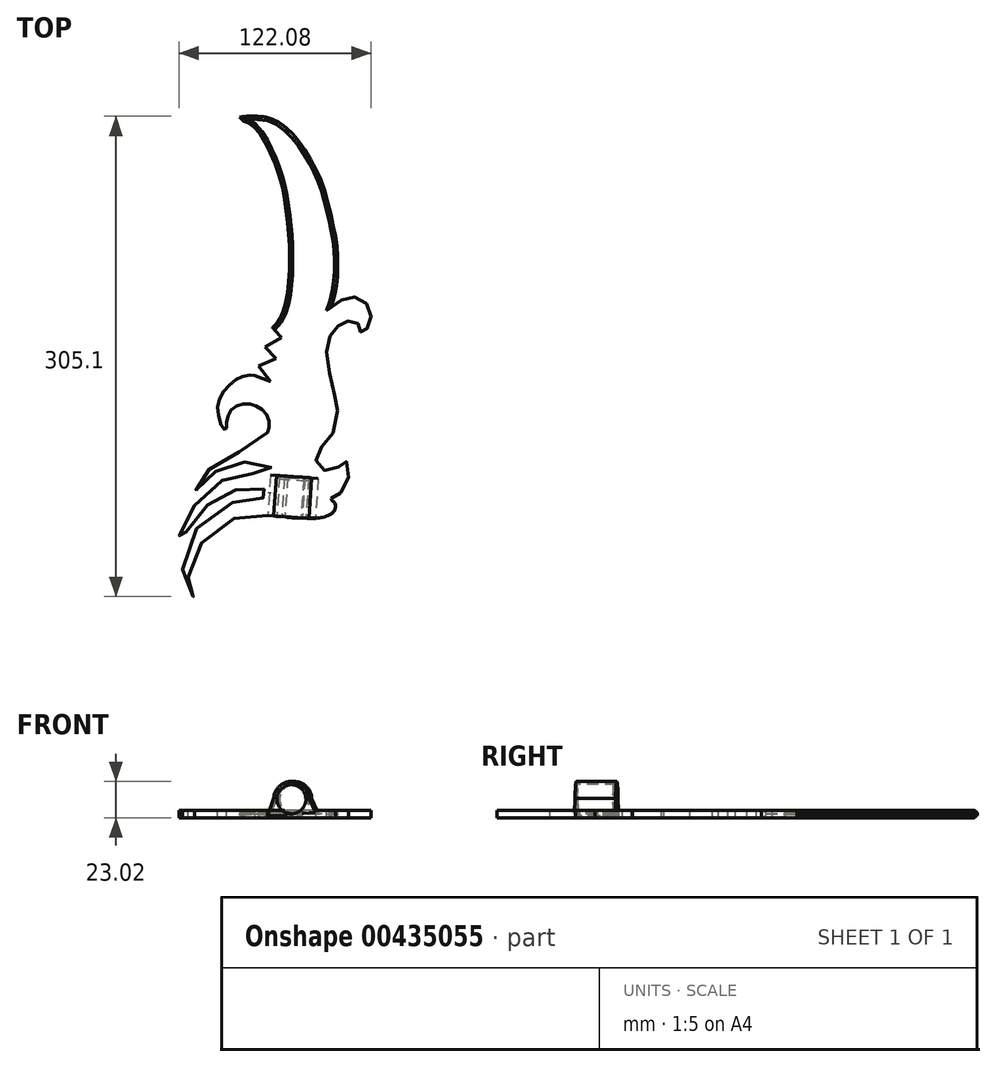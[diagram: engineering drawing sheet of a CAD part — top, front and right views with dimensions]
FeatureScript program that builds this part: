
annotation { "Feature Type Name" : "Feature", "Feature Type Description" : "" }
export const myFeature = defineFeature(function(context is Context, id is Id, definition is map)
    precondition{}
    {
        {
            var Q0;
            Q0=qCreatedBy(makeId("Top.planeOp"),FACE);
            var sketch = newSketch(context, id + "F0", { "sketchPlane" : qUnion([Q0])});
            skFitSpline(sketch, "E0", {"points": [v(-34.12, 66.89) * mm, v(-30.2, 66.33) * mm, v(-25.4, 63.2) * mm, v(-21.03, 57.83) * mm, v(-16.78, 49.66) * mm, v(-14.1, 40.04) * mm, v(-12.64, 32.43) * mm, v(-12.52, 25.04) * mm, v(-13.23, 19.62) * mm, v(-14.2, 16.34) * mm], "startDerivative": vector(44.42, -1.57) * mm, "endDerivative": vector(-12.95, -38.23) * mm});
            skPoint(sketch, "E1.1.internal.orphan", {"position": v(-37.5, 65.72) * mm});
            skFitSpline(sketch, "E2", {"points": [v(-38.79, 67.2) * mm, v(-37.5, 65.72) * mm, v(-36.06, 65.1) * mm, v(-33.67, 63.13) * mm, v(-30.7, 58) * mm, v(-27.58, 49.9) * mm, v(-26.1, 41.97) * mm, v(-25.34, 34.51) * mm, v(-25.23, 26.4) * mm, v(-25.88, 18.94) * mm, v(-27.1, 14.66) * mm, v(-28.52, 12.14) * mm, v(-29.72, 10.93) * mm], "startDerivative": vector(21.85, -34.76) * mm, "endDerivative": vector(-24.35, -21.3) * mm});
            skFitSpline(sketch, "E3", {"points": [v(-14.2, 16.34) * mm, v(-11.75, 18.07) * mm, v(-10.11, 18.83) * mm, v(-8.76, 19.09) * mm, v(-7.2, 18.94) * mm, v(-5.63, 18.1) * mm, v(-4.5, 16.83) * mm, v(-3.8, 15.3) * mm, v(-3.63, 13.44) * mm, v(-3.88, 11.8) * mm, v(-4.57, 10.78) * mm, v(-5.27, 10.09) * mm, v(-5.74, 9.8) * mm, v(-6, 9.8) * mm, v(-6.34, 9.82) * mm, v(-6.43, 10.45) * mm, v(-6.54, 11.07) * mm, v(-6.83, 11.84) * mm, v(-7.56, 12.35) * mm, v(-8.47, 12.64) * mm, v(-9.5, 12.68) * mm, v(-10.3, 12.57) * mm, v(-11.24, 12.1) * mm, v(-12.26, 11.36) * mm, v(-13.23, 10.51) * mm, v(-14.2, 9.17) * mm, v(-14.93, 7.68) * mm, v(-15.33, 5) * mm, v(-15.23, 1.86) * mm, v(-14.2, -3.06) * mm, v(-13.23, -7.05) * mm, v(-12.9, -8.43) * mm, v(-12.52, -11.23) * mm, v(-13.23, -15.98) * mm, v(-15.36, -19.12) * mm, v(-16.89, -20.78) * mm, v(-17.93, -22.74) * mm, v(-18.22, -24.24) * mm, v(-17.58, -25.63) * mm, v(-16.2, -26.78) * mm, v(-14.2, -26.84) * mm, v(-12.52, -26.15) * mm, v(-11.3, -24.94) * mm, v(-10.66, -24.36) * mm, v(-10.26, -24.47) * mm, v(-9.85, -25) * mm, v(-9.54, -27.67) * mm, v(-10.36, -31) * mm, v(-11.79, -32.93) * mm, v(-13.23, -33.8) * mm, v(-13.85, -34.06) * mm, v(-14.2, -34.26) * mm], "startDerivative": vector(93.5, 70.38) * mm, "endDerivative": vector(-33.1, -21.45) * mm});
            skFitSpline(sketch, "E4", {"points": [v(-14.2, -34.26) * mm, v(-13.85, -34.86) * mm, v(-13.23, -35.4) * mm, v(-13.23, -37.2) * mm, v(-14.2, -38.33) * mm, v(-16.2, -39.21) * mm, v(-17.39, -39.39) * mm, v(-18.27, -39.43) * mm, v(-24.8, -39.34) * mm, v(-26.28, -39.12) * mm], "startDerivative": vector(3.21, -10.85) * mm, "endDerivative": vector(-9.82, 2.35) * mm});
            skFitSpline(sketch, "E5", {"points": [v(-30.95, -38.8) * mm, v(-32.5, -38.64) * mm, v(-37.41, -38.8) * mm, v(-43.54, -41.43) * mm, v(-47.73, -45.01) * mm, v(-50.64, -49.87) * mm, v(-51.99, -54.28) * mm, v(-51.99, -57.42) * mm, v(-51.24, -59.21) * mm, v(-50.42, -59.81) * mm, v(-50.57, -60.2) * mm, v(-52.11, -59.28) * mm, v(-53.35, -55.97) * mm, v(-53.34, -50.93) * mm, v(-51, -44.17) * mm, v(-46.77, -38.9) * mm, v(-40.46, -35.43) * mm, v(-36.19, -34.43) * mm, v(-33.16, -34.16) * mm, v(-31.58, -33.95) * mm, v(-30.95, -33.58) * mm, v(-30.6, -33.08) * mm, v(-30.6, -32.44) * mm, v(-31.44, -31.94) * mm, v(-33.03, -31.53) * mm, v(-35.65, -31.5) * mm, v(-39.22, -31.94) * mm, v(-42.65, -33.18) * mm, v(-45.37, -34.8) * mm, v(-49, -38.13) * mm, v(-51.63, -41.29) * mm, v(-53.1, -44.37) * mm, v(-53.85, -46.14) * mm, v(-54.2, -46.14) * mm, v(-54.48, -45.56) * mm, v(-54.02, -42.88) * mm, v(-52.77, -39.98) * mm, v(-50.27, -36) * mm, v(-46.6, -31.99) * mm, v(-42.67, -29.3) * mm, v(-39.9, -28.26) * mm, v(-35.7, -27.7) * mm, v(-32.65, -27.57) * mm, v(-30.95, -27.36) * mm, v(-30.6, -26.88) * mm, v(-30.1, -26.18) * mm, v(-30.6, -25.5) * mm, v(-32.79, -24.8) * mm, v(-36.59, -24.66) * mm, v(-40.25, -25.01) * mm, v(-43.3, -26.12) * mm, v(-46, -28.15) * mm, v(-48.19, -30.27) * mm, v(-49.72, -31.71) * mm, v(-50.14, -32.07) * mm, v(-50.2, -31.23) * mm, v(-48.74, -29.13) * mm, v(-45.78, -25.77) * mm, v(-42.4, -23.42) * mm, v(-37.97, -21.83) * mm, v(-34.3, -20.59) * mm, v(-30.95, -16.86) * mm], "startDerivative": vector(-108.57, 14) * mm, "endDerivative": vector(144.74, 200.6) * mm});
            skFitSpline(sketch, "E6", {"points": [v(-30.95, -16.86) * mm, v(-30.6, -15.52) * mm, v(-30.6, -13.7) * mm, v(-31.61, -11.57) * mm, v(-33.33, -10.12) * mm, v(-35.2, -9.35) * mm, v(-37.46, -9.22) * mm, v(-39.59, -9.94) * mm, v(-41.13, -11.53) * mm, v(-41.72, -13.57) * mm, v(-41.9, -15.15) * mm, v(-41.95, -15.83) * mm, v(-42.26, -16.02) * mm, v(-42.8, -15.6) * mm, v(-44.08, -12.16) * mm, v(-44, -8.86) * mm, v(-42.62, -5.9) * mm, v(-39.93, -3.27) * mm, v(-37.63, -2) * mm, v(-35.27, -1.62) * mm, v(-34.45, -1.78) * mm], "startDerivative": vector(9.27, 30.68) * mm, "endDerivative": vector(21.42, -6.86) * mm});
            skLineSegment(sketch, "E7", {"start": v(-34.45, -1.78) * mm, "end": v(-30.16, -3.32) * mm});
            skLineSegment(sketch, "E8", {"start": v(-30.16, -3.32) * mm, "end": v(-33.35, 0.74) * mm});
            skLineSegment(sketch, "E9", {"start": v(-33.35, 0.74) * mm, "end": v(-28.74, 2.77) * mm});
            skLineSegment(sketch, "E10", {"start": v(-28.74, 2.77) * mm, "end": v(-31.7, 5.8) * mm});
            skLineSegment(sketch, "E11", {"start": v(-31.7, 5.8) * mm, "end": v(-27.33, 8.32) * mm});
            skLineSegment(sketch, "E12", {"start": v(-27.33, 8.32) * mm, "end": v(-29.72, 10.93) * mm});
            skFitSpline(sketch, "E13", {"points": [v(-30.95, -16.86) * mm, v(-30.6, -15.52) * mm, v(-30.6, -13.7) * mm, v(-31.61, -11.57) * mm, v(-33.33, -10.12) * mm, v(-35.2, -9.35) * mm, v(-37.46, -9.22) * mm, v(-39.59, -9.94) * mm, v(-41.13, -11.53) * mm, v(-41.72, -13.57) * mm, v(-41.9, -15.15) * mm, v(-41.95, -15.83) * mm, v(-42.26, -16.02) * mm, v(-42.8, -15.6) * mm, v(-44.08, -12.16) * mm, v(-44, -8.86) * mm, v(-42.62, -5.9) * mm, v(-39.93, -3.27) * mm, v(-37.63, -2) * mm, v(-35.27, -1.62) * mm, v(-34.45, -1.78) * mm], "startDerivative": vector(9.27, 30.68) * mm, "endDerivative": vector(21.42, -6.86) * mm});
            skFitSpline(sketch, "E14", {"points": [v(-34.12, 66.89) * mm, v(-36.24, 66.89) * mm, v(-38.96, 66.58) * mm], "startDerivative": vector(-4.4, 0.14) * mm, "endDerivative": vector(-5.27, -0.73) * mm});
            skLineSegment(sketch, "E15", {"start": v(-30.95, -38.8) * mm, "end": v(-26.28, -39.12) * mm});
            skSolve(sketch);
        }
        {
            var Q0;
            Q0=makeQuery(id+"F0.imprint","IMPRINT",FACE,{"disambiguationData":[TD([[makeQuery(id+"F0.imprint","IMPRINT",EDGE,{"derivedFrom":sQuery(id+"F0.wireOp",EDGE,"E0")}),-1.0]])]});
            extrude(context, id + "F1", {"entities" : qUnion([Q0]), "depth" : 2 * mm});
        }
        {
            var Q0;
            Q0=qCreatedBy(makeId("Front.planeOp"),FACE);
            cPlane(context, id + "F2", {"entities" : qUnion([Q0]), "cplaneType" : CPlaneType.OFFSET, "offset" : 27.9 * mm, "width" : 150 * mm, "height" : 150 * mm});
        }
        {
            var Q0;
            Q0=makeQuery(id+"F1.opExtrude","SWEPT_BODY",BODY,{"disambiguationData":[OSD([sQuery(id+"F0.wireOp",EDGE,"E0"),sQuery(id+"F0.wireOp",EDGE,"E2"),sQuery(id+"F0.wireOp",EDGE,"E3"),sQuery(id+"F0.wireOp",EDGE,"E4"),sQuery(id+"F0.wireOp",EDGE,"E5"),sQuery(id+"F0.wireOp",EDGE,"E6"),sQuery(id+"F0.wireOp",EDGE,"E7"),sQuery(id+"F0.wireOp",EDGE,"E8"),sQuery(id+"F0.wireOp",EDGE,"E9"),sQuery(id+"F0.wireOp",EDGE,"E10"),sQuery(id+"F0.wireOp",EDGE,"E11"),sQuery(id+"F0.wireOp",EDGE,"E12"),sQuery(id+"F0.wireOp",EDGE,"E3"),sQuery(id+"F0.wireOp",EDGE,"E3"),sQuery(id+"F0.wireOp",EDGE,"E5"),sQuery(id+"F0.wireOp",EDGE,"E5"),sQuery(id+"F0.wireOp",EDGE,"E5"),sQuery(id+"F0.wireOp",EDGE,"E5"),sQuery(id+"F0.wireOp",EDGE,"E5"),sQuery(id+"F0.wireOp",EDGE,"E13"),sQuery(id+"F0.wireOp",EDGE,"E14"),sQuery(id+"F0.wireOp",EDGE,"E15")])]});
            var Q1;
            Q1=qCreatedBy(makeId("Origin.pointOp"),VERTEX);
            transform(context, id + "F3", {"entities" : qUnion([Q0]), "transformType" : TransformType.SCALE_UNIFORMLY, "scale" : 2.4, "scalePoint" : qUnion([Q1]), "makeCopy" : false});
        }
        {
            var Q0;
            Q0=makeQuery(id+"F1.opExtrude","SWEPT_FACE",FACE,{"disambiguationData":[OSD([sQuery(id+"F0.wireOp",EDGE,"E15")])]});
            var sketch = newSketch(context, id + "F4", { "sketchPlane" : qUnion([Q0])});
            skCircle(sketch, "E16", {"center": v(-52.8, 10.47) * mm, "radius": 9.25 * mm});
            skPoint(sketch, "E17.orphan", {"position": v(-62.2, 4.8) * mm});
            skCircle(sketch, "E18.0", {"center": v(-52.8, 10.47) * mm, "radius": 11.25 * mm});
            skLineSegment(sketch, "E19", {"start": v(-64.04, 11.1) * mm, "end": v(-67.83, 0) * mm});
            skLineSegment(sketch, "E20", {"start": v(-67.83, 0) * mm, "end": v(-56.94, 0) * mm});
            skLineSegment(sketch, "E21", {"start": v(-41.57, 10.9) * mm, "end": v(-37.48, 2.02) * mm});
            skLineSegment(sketch, "E22", {"start": v(-37.48, 2.02) * mm, "end": v(-45.92, 1.57) * mm});
            skSolve(sketch);
        }
        {
            var Q0;
            Q0 = qSketchRegion(id + "F4", true);
            extrude(context, id + "F5", {"entities" : qUnion([Q0]), "oppositeDirection" : true, "depth" : 25.8 * mm});
        }
        {
            var Q0;
            Q0=makeQuery(id+"F5.opExtrude","SWEPT_BODY",BODY,{"disambiguationData":[OSD([sQuery(id+"F4.wireOp",EDGE,"E16"),sQuery(id+"F4.wireOp",EDGE,"E18.0")])]});
            transform(context, id + "F6", {"entities" : qUnion([Q0]), "transformType" : TransformType.TRANSLATION_3D, "dx" : 0 * mm, "dy" : 0 * mm, "dz" : 1.3 * mm, "makeCopy" : false});
        }
        {
            var Q0;
            Q0=makeQuery(id+"F5.opExtrude","CAP_FACE",FACE,{"disambiguationData":[OSD([sQuery(id+"F4.wireOp",EDGE,"E16"),sQuery(id+"F4.wireOp",EDGE,"E18.0")])],"isStart":true});
            var sketch = newSketch(context, id + "F7", { "sketchPlane" : qUnion([Q0])});
            skCircle(sketch, "E23", {"center": v(-52.8, 11.77) * mm, "radius": 9.25 * mm});
            skSolve(sketch);
        }
        {
            var Q0;
            Q0 = qSketchRegion(id + "F7", true);
            extrude(context, id + "F8", {"entities" : qUnion([Q0]), "operationType" : NewBodyOperationType.REMOVE, "endBound" : BoundingType.SYMMETRIC, "oppositeDirection" : true, "depth" : 50 * mm});
        }
        {
            var Q0;
            Q0=makeQuery(id+"F5.opExtrude","CAP_FACE",FACE,{"disambiguationData":[OSD([sQuery(id+"F4.wireOp",EDGE,"E16"),sQuery(id+"F4.wireOp",EDGE,"E18.0"),sQuery(id+"F4.wireOp",EDGE,"E19"),sQuery(id+"F4.wireOp",EDGE,"E20"),sQuery(id+"F4.wireOp",EDGE,"E21"),sQuery(id+"F4.wireOp",EDGE,"E22")])],"isStart":false});
            var sketch = newSketch(context, id + "F9", { "sketchPlane" : qUnion([Q0])});
            skCircle(sketch, "E24", {"center": v(52.8, 11.77) * mm, "radius": 9.8 * mm});
            skSolve(sketch);
        }
        {
            var Q0;
            Q0 = qSketchRegion(id + "F9", true);
            extrude(context, id + "F10", {"entities" : qUnion([Q0]), "oppositeDirection" : true, "depth" : 2 * mm});
        }
        {
            var Q0;
            Q0=makeQuery(id+"F1.opExtrude","CAP_EDGE",EDGE,{"disambiguationData":[OSD([sQuery(id+"F0.wireOp",EDGE,"E0")])],"isStart":false});
            var Q1;
            Q1=makeQuery(id+"F1.opExtrude","CAP_EDGE",EDGE,{"disambiguationData":[OSD([sQuery(id+"F0.wireOp",EDGE,"E0")])],"isStart":true});
            var Q2;
            Q2=makeQuery(id+"F1.opExtrude","CAP_EDGE",EDGE,{"disambiguationData":[OSD([sQuery(id+"F0.wireOp",EDGE,"E2")])],"isStart":false});
            var Q3;
            Q3=makeQuery(id+"F1.opExtrude","CAP_EDGE",EDGE,{"disambiguationData":[OSD([sQuery(id+"F0.wireOp",EDGE,"E2")])],"isStart":true});
            chamfer(context, id + "F11", {"entities" : qUnion([Q0, Q1, Q2, Q3]), "width" : 2 * mm, "tangentPropagation" : true});
        }
    });
